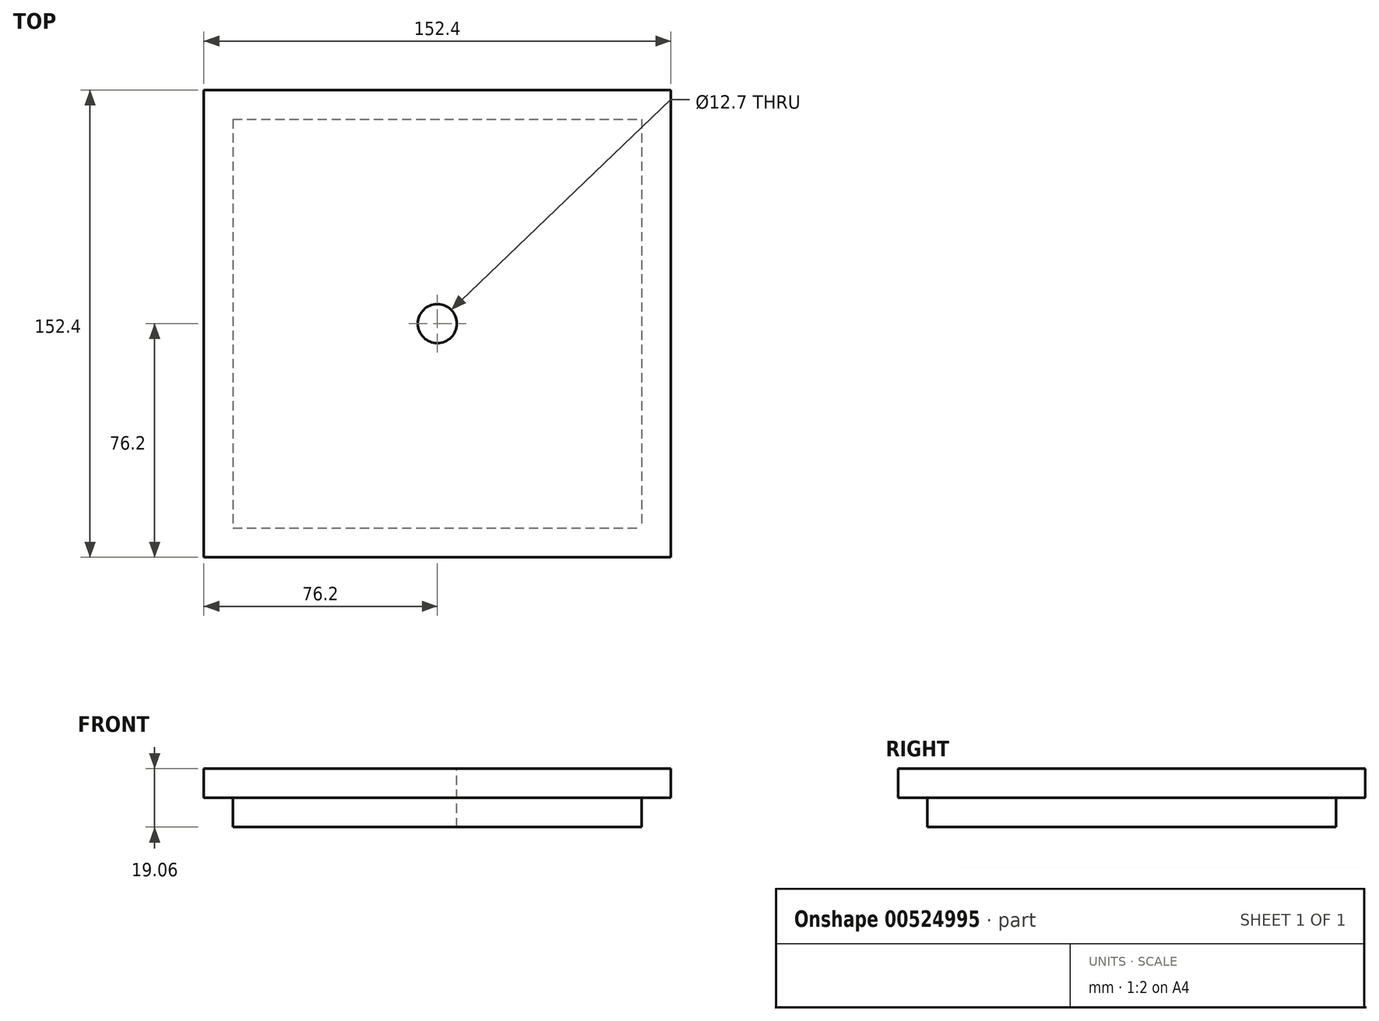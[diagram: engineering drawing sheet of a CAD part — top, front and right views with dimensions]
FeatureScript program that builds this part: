
annotation { "Feature Type Name" : "Feature", "Feature Type Description" : "" }
export const myFeature = defineFeature(function(context is Context, id is Id, definition is map)
    precondition{}
    {
        {
            var Q0;
            Q0=qCreatedBy(makeId("Top.planeOp"),FACE);
            var sketch = newSketch(context, id + "F0", { "sketchPlane" : qUnion([Q0])});
            skLineSegment(sketch, "E0.bottom", {"start": v(-76.2, -76.2) * mm, "end": v(76.2, -76.2) * mm});
            skLineSegment(sketch, "E0.top", {"start": v(-76.2, 76.2) * mm, "end": v(76.2, 76.2) * mm});
            skLineSegment(sketch, "E0.left", {"start": v(-76.2, -76.2) * mm, "end": v(-76.2, 76.2) * mm});
            skLineSegment(sketch, "E0.right", {"start": v(76.2, -76.2) * mm, "end": v(76.2, 76.2) * mm});
            skPoint(sketch, "E0.middle", {"position": v(0, 0) * mm});
            skSolve(sketch);
        }
        {
            var Q0;
            Q0=makeQuery(id+"F0.imprint","IMPRINT",FACE,{"disambiguationData":[TD([[makeQuery(id+"F0.imprint","IMPRINT",EDGE,{"derivedFrom":sQuery(id+"F0.wireOp",EDGE,"E0.bottom")}),1.0]])]});
            extrude(context, id + "F1", {"entities" : qUnion([Q0]), "depth" : 9.52 * mm, "offsetDistance" : 25.4 * mm});
        }
        {
            var Q0;
            Q0=makeQuery(id+"F1.opExtrude","CAP_FACE",FACE,{"disambiguationData":[OSD([sQuery(id+"F0.wireOp",EDGE,"E0.bottom"),sQuery(id+"F0.wireOp",EDGE,"E0.top"),sQuery(id+"F0.wireOp",EDGE,"E0.left"),sQuery(id+"F0.wireOp",EDGE,"E0.right")])],"isStart":true});
            var sketch = newSketch(context, id + "F2", { "sketchPlane" : qUnion([Q0])});
            skLineSegment(sketch, "E1.bottom", {"start": v(-66.67, -66.68) * mm, "end": v(66.68, -66.68) * mm});
            skLineSegment(sketch, "E1.top", {"start": v(-66.67, 66.68) * mm, "end": v(66.68, 66.68) * mm});
            skLineSegment(sketch, "E1.left", {"start": v(-66.67, -66.68) * mm, "end": v(-66.67, 66.68) * mm});
            skLineSegment(sketch, "E1.right", {"start": v(66.67, -66.68) * mm, "end": v(66.67, 66.68) * mm});
            skPoint(sketch, "E1.middle", {"position": v(0, 0) * mm});
            skSolve(sketch);
        }
        {
            var Q0;
            Q0 = qSketchRegion(id + "F2", true);
            extrude(context, id + "F3", {"entities" : qUnion([Q0]), "operationType" : NewBodyOperationType.ADD, "depth" : 9.52 * mm, "offsetDistance" : 25.4 * mm});
        }
        {
            var Q0;
            Q0=makeQuery(id+"F1.opExtrude","CAP_FACE",FACE,{"disambiguationData":[OSD([sQuery(id+"F0.wireOp",EDGE,"E0.bottom"),sQuery(id+"F0.wireOp",EDGE,"E0.top"),sQuery(id+"F0.wireOp",EDGE,"E0.left"),sQuery(id+"F0.wireOp",EDGE,"E0.right")])],"isStart":false});
            var sketch = newSketch(context, id + "F4", { "sketchPlane" : qUnion([Q0])});
            skPoint(sketch, "E2", {"position": v(0, 0) * mm});
            skSolve(sketch);
        }
        {
            var Q0;
            Q0=sQuery(id+"F4.wireOp",VERTEX,"E2");
            var Q1;
            Q1=makeQuery(id+"F1.opExtrude","SWEPT_BODY",BODY,{"disambiguationData":[OSD([sQuery(id+"F0.wireOp",EDGE,"E0.bottom"),sQuery(id+"F0.wireOp",EDGE,"E0.top"),sQuery(id+"F0.wireOp",EDGE,"E0.left"),sQuery(id+"F0.wireOp",EDGE,"E0.right")])]});
            hole(context, id + "F5", {"style" : HoleStyle.SIMPLE, "endStyle" : HoleEndStyle.THROUGH, "holeDiameter" : 12.7 * mm, "isTappedThrough" : true, "tappedDepth" : 12.7 * mm, "tapClearance" : 3, "locations" : qUnion([Q0]), "scope" : qUnion([Q1])});
        }
    });
